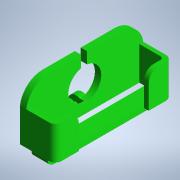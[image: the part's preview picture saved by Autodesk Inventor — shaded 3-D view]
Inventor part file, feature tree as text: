
AUTODESK INVENTOR PART (.ipt)
format: ipt  version: 2022 (Build 260153000, 153)  size: 278,528 bytes
history: native  units: mm
features: extrude x12, sketch x12, reference x7, other x5, fillet x4, projected_geometry x4
ambient origin geometry x8: Origin, YZ Plane, XZ Plane, XY Plane, X Axis, Y Axis, Z Axis, Center Point
bodies: Body1 (feature_tree)
feature tree (44):
  other  "Твердое тело1"
  extrude  "Выдавливание1"  Depth=4.0mm TaperAngle=0.0deg
  extrude  "Выдавливание2"  Depth=4.0mm
  extrude  "Выдавливание3"  Depth=4.5mm
  extrude  "Выдавливание4"  Depth=3.0mm TaperAngle=0.0deg
  extrude  "Выдавливание5"  Depth=4.0mm TaperAngle=0.0deg
  extrude  "Выдавливание6"  Depth=3.0mm
  extrude  "Выдавливание7"  Depth=3.0mm
  extrude  "Выдавливание8"  Depth=4.0mm TaperAngle=0.0deg
  fillet  "Сопряжение1"  Radius=4.0mm
  extrude  "Выдавливание9"  Depth=2.5mm
  fillet  "Сопряжение2"  Radius=2.5mm
  fillet  "Сопряжение3"  Radius=15.5mm
  fillet  "Сопряжение4"  Radius=15.5mm
  extrude  "Выдавливание10"  Depth=4.0mm TaperAngle=0.0deg
  extrude  "Выдавливание11"  Depth=4.0mm
  extrude  "Выдавливание12"  Depth=3.0mm
  sketch  "Эскиз1"
  reference  "Ссылка1"
  sketch  "Эскиз2"
  projected_geometry  "Спроецированная петля1"
  sketch  "Эскиз3"
  projected_geometry  "Спроецированная петля2"
  sketch  "Эскиз4"
  reference  "Ссылка2"
  reference  "Ссылка3"
  reference  "Ссылка4"
  reference  "Ссылка5"
  reference  "Ссылка6"
  sketch  "Эскиз5"
  reference  "Ссылка7"
  sketch  "Эскиз6"
  projected_geometry  "Спроецированная петля3"
  sketch  "Эскиз7"
  sketch  "Эскиз8"
  sketch  "Эскиз9"
  sketch  "Эскиз10"
  sketch  "Эскиз11"
  projected_geometry  "Спроецированная петля4"
  sketch  "Эскиз12"
  other  "<path> - Robot.iam"
  other  "000.000 - Robot.iam"
  other  "camera_holder:1"
  other  "C525:1"
note: 1 file-system path scrubbed to <path> (originals preserved in map.json)
